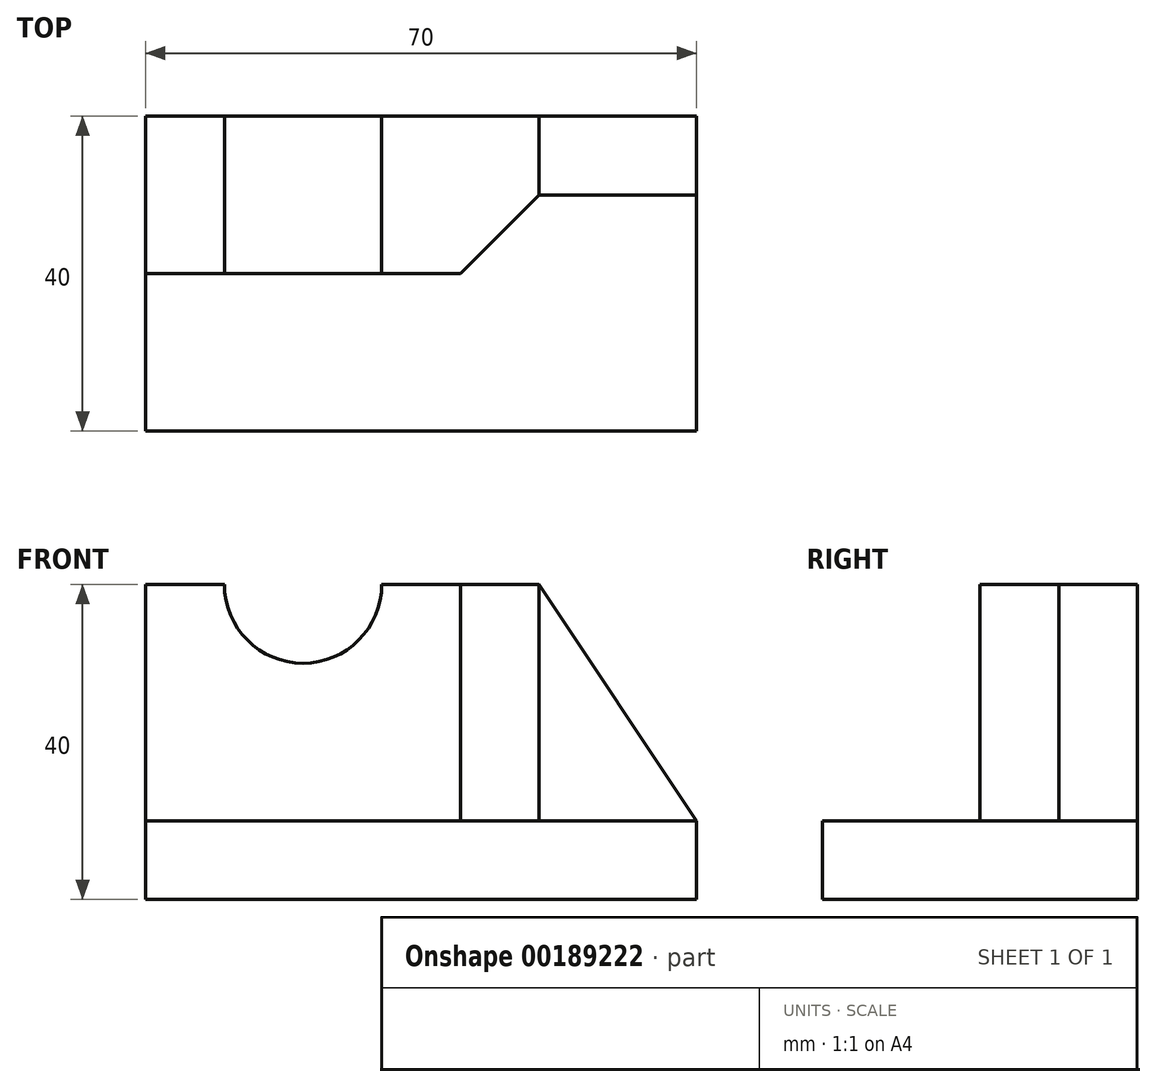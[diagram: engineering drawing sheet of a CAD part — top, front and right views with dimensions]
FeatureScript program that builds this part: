
annotation { "Feature Type Name" : "Feature", "Feature Type Description" : "" }
export const myFeature = defineFeature(function(context is Context, id is Id, definition is map)
    precondition{}
    {
        {
            var Q0;
            Q0=qCreatedBy(makeId("Top.planeOp"),FACE);
            var sketch = newSketch(context, id + "F0", { "sketchPlane" : qUnion([Q0])});
            skLineSegment(sketch, "E0.bottom", {"start": v(0, 0) * mm, "end": v(70, 0) * mm});
            skLineSegment(sketch, "E0.top", {"start": v(0, 40) * mm, "end": v(70, 40) * mm});
            skLineSegment(sketch, "E0.left", {"start": v(0, 0) * mm, "end": v(0, 40) * mm});
            skLineSegment(sketch, "E0.right", {"start": v(70, 0) * mm, "end": v(70, 40) * mm});
            skSolve(sketch);
        }
        {
            var Q0;
            Q0 = qSketchRegion(id + "F0", true);
            extrude(context, id + "F1", {"entities" : qUnion([Q0]), "depth" : 40 * mm});
        }
        {
            var Q0;
            Q0=makeQuery(id+"F1.opExtrude","CAP_FACE",FACE,{"disambiguationData":[OSD([sQuery(id+"F0.wireOp",EDGE,"E0.bottom"),sQuery(id+"F0.wireOp",EDGE,"E0.top"),sQuery(id+"F0.wireOp",EDGE,"E0.left"),sQuery(id+"F0.wireOp",EDGE,"E0.right")])],"isStart":false});
            var sketch = newSketch(context, id + "F2", { "sketchPlane" : qUnion([Q0])});
            skLineSegment(sketch, "E1", {"start": v(0, 20) * mm, "end": v(40, 20) * mm});
            skLineSegment(sketch, "E2", {"start": v(40, 20) * mm, "end": v(50, 30) * mm});
            skLineSegment(sketch, "E3", {"start": v(50, 30) * mm, "end": v(70, 30) * mm});
            skLineSegment(sketch, "E4.0", {"start": v(0, 0) * mm, "end": v(0, 20) * mm});
            skLineSegment(sketch, "E5.0", {"start": v(0, 0) * mm, "end": v(70, 0) * mm});
            skLineSegment(sketch, "E6.0", {"start": v(70, 0) * mm, "end": v(70, 30) * mm});
            skPoint(sketch, "E7.orphan", {"position": v(0, 40) * mm});
            skPoint(sketch, "E8.orphan", {"position": v(70, 40) * mm});
            skSolve(sketch);
        }
        {
            var Q0;
            Q0=makeQuery(id+"F2.imprint","IMPRINT",FACE,{"disambiguationData":[TD([[makeQuery(id+"F2.imprint","IMPRINT",EDGE,{"derivedFrom":sQuery(id+"F2.wireOp",EDGE,"E1")}),-1.0]])]});
            extrude(context, id + "F3", {"entities" : qUnion([Q0]), "operationType" : NewBodyOperationType.REMOVE, "oppositeDirection" : true, "depth" : 30 * mm});
        }
        {
            var Q0;
            Q0=makeQuery(id+"F1.opExtrude","CAP_EDGE",EDGE,{"disambiguationData":[OSD([sQuery(id+"F0.wireOp",EDGE,"E0.right")])],"isStart":false});
            chamfer(context, id + "F4", {"entities" : qUnion([Q0]), "chamferType" : ChamferType.TWO_OFFSETS, "width1" : 20 * mm, "oppositeDirection" : false, "width2" : 30 * mm, "tangentPropagation" : true});
        }
        {
            var Q0;
            Q0=makeQuery(id+"F3.boolean.opBoolean","COPY",FACE,{"derivedFrom":makeQuery(id+"F3.opExtrude","SWEPT_FACE",FACE,{"disambiguationData":[OSD([sQuery(id+"F2.wireOp",EDGE,"E1")])]})});
            var sketch = newSketch(context, id + "F5", { "sketchPlane" : qUnion([Q0])});
            skArc(sketch, "E9", {"start": v(10, 40) * mm, "mid": v(20, 30) * mm, "end": v(30, 40) * mm});
            skLineSegment(sketch, "E10.0", {"start": v(10, 40) * mm, "end": v(30, 40) * mm});
            skPoint(sketch, "E11.orphan", {"position": v(0, 40) * mm});
            skPoint(sketch, "E12.orphan", {"position": v(40, 40) * mm});
            skSolve(sketch);
        }
        {
            var Q0;
            Q0=makeQuery(id+"F5.imprint","IMPRINT",FACE,{"disambiguationData":[TD([[makeQuery(id+"F5.imprint","IMPRINT",EDGE,{"derivedFrom":sQuery(id+"F5.wireOp",EDGE,"E9")}),1.0]])]});
            extrude(context, id + "F6", {"entities" : qUnion([Q0]), "operationType" : NewBodyOperationType.REMOVE, "endBound" : BoundingType.UP_TO_NEXT, "oppositeDirection" : true, "depth" : 25 * mm});
        }
    });
